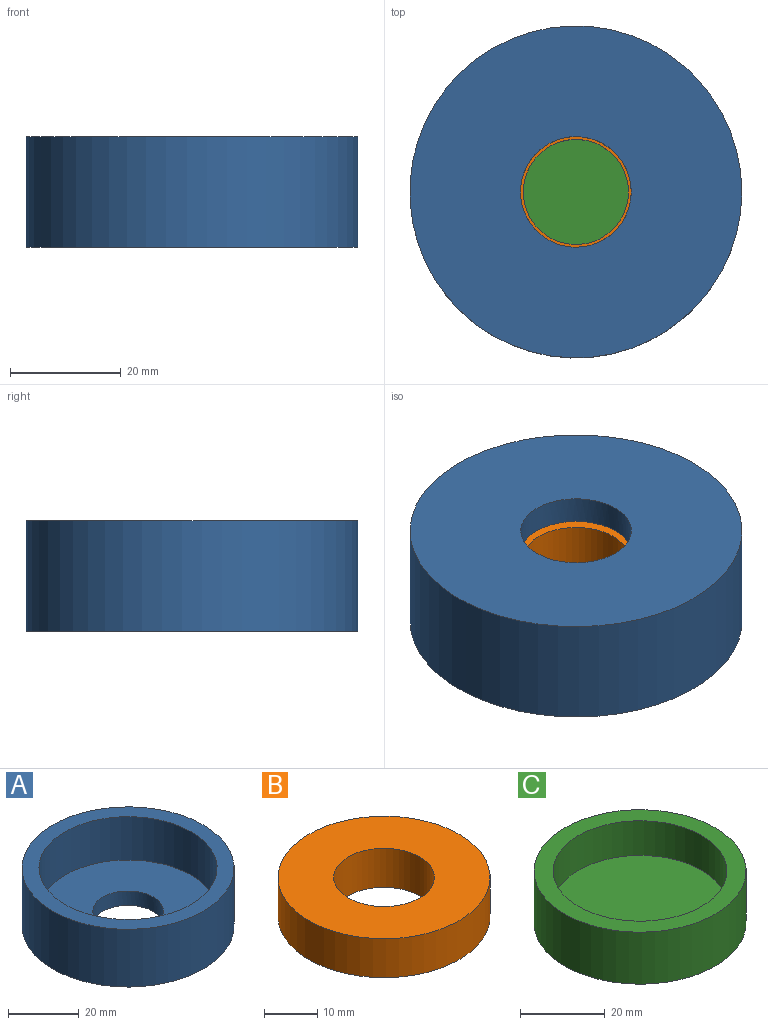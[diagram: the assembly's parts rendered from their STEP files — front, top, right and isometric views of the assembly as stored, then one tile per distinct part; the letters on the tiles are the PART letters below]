
ASSEMBLY  parts=3 mates=2
PART A: 6 faces, bbox 60x60x20 mm
  f0: cylinder r=30mm len=60mm, axis (0,0,-1), area 3769.9mm2, adj f1,f3
  f1: plane 60x60mm, normal (0,0,-1), area 2513.3mm2, adj f0,f5
  f2: cylinder r=25.2mm len=50.4mm, axis (0,0,-1), area 2375mm2, adj f3,f4
  f3: plane 60x60mm, normal (0,0,1), area 832.4mm2, adj f0,f2
  f4: plane 50.4x50.4mm, normal (0,0,1), area 1680.9mm2, adj f2,f5
  f5: cylinder r=10mm len=20mm, axis (0,0,-1), area 314.2mm2, adj f1,f4
PART B: 4 faces, bbox 40x40x9 mm
  f0: cylinder r=9.5mm len=19mm, axis (0,0,-1), area 537.2mm2, adj f2,f3
  f1: cylinder r=20mm len=40mm, axis (0,0,-1), area 1131mm2, adj f2,f3
  f2: plane 40x40mm, normal (0,0,1), area 973.1mm2, adj f0,f1
  f3: plane 40x40mm, normal (0,0,-1), area 973.1mm2, adj f0,f1
PART C: 5 faces, bbox 50x50x15 mm
  f0: cylinder r=25mm len=50mm, axis (0,0,-1), area 2356.2mm2, adj f1,f3
  f1: plane 50x50mm, normal (0,0,-1), area 1963.5mm2, adj f0
  f2: cylinder r=20.5mm len=41mm, axis (0,0,-1), area 1288.1mm2, adj f3,f4
  f3: plane 50x50mm, normal (0,0,1), area 643.2mm2, adj f0,f2
  f4: plane 41x41mm, normal (0,0,1), area 1320.3mm2, adj f2
PLACE A rot(axis=(1,0,0),180deg) t=(0,0,20)mm
PLACE B t=(0,0,5)mm
PLACE C at identity
MATE fastened B.f0 <-> C.f2  axis (0,0,1) through (0,0,5)mm
MATE fastened A.f5 <-> B.f0  axis (0,0,-1) through (0,0,20)mm
